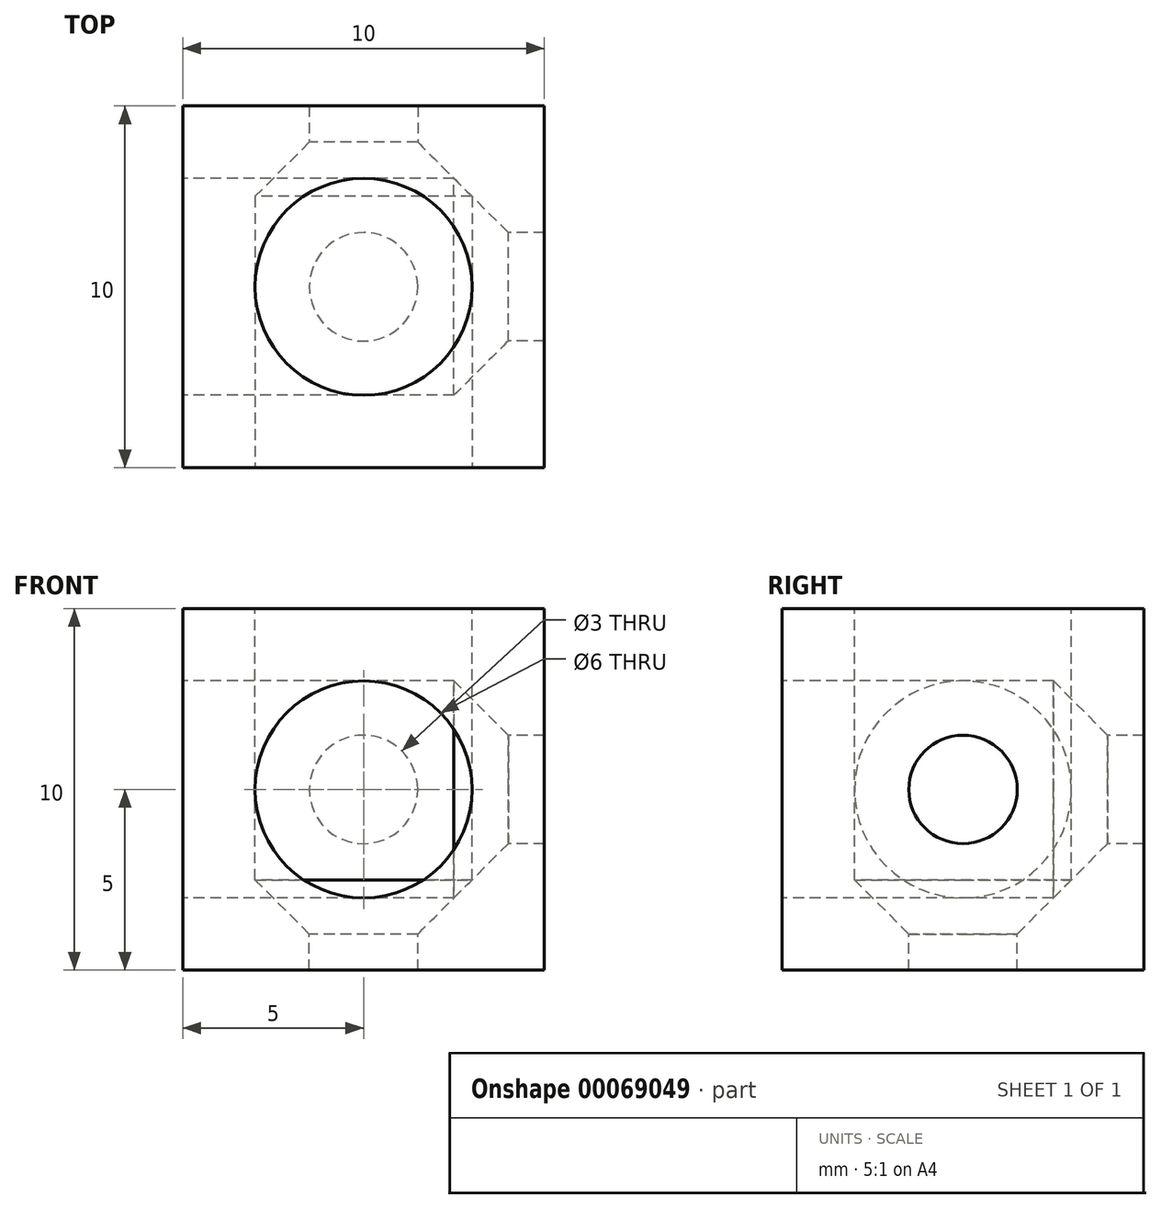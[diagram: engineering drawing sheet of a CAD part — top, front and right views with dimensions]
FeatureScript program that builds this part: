
annotation { "Feature Type Name" : "Feature", "Feature Type Description" : "" }
export const myFeature = defineFeature(function(context is Context, id is Id, definition is map)
    precondition{}
    {
        {
            var Q0;
            Q0=qCreatedBy(makeId("Front.planeOp"),FACE);
            var sketch = newSketch(context, id + "F0", { "sketchPlane" : qUnion([Q0])});
            skLineSegment(sketch, "E0.rect.bottom", {"start": v(5, 5) * mm, "end": v(-5, 5) * mm});
            skLineSegment(sketch, "E0.rect.top", {"start": v(5, -5) * mm, "end": v(-5, -5) * mm});
            skLineSegment(sketch, "E0.rect.left", {"start": v(5, 5) * mm, "end": v(5, -5) * mm});
            skLineSegment(sketch, "E0.rect.right", {"start": v(-5, 5) * mm, "end": v(-5, -5) * mm});
            skPoint(sketch, "E0.rect.middle", {"position": v(0, 0) * mm});
            skSolve(sketch);
        }
        {
            var Q0;
            Q0=makeQuery(id+"F0.imprint","IMPRINT",FACE,{"disambiguationData":[TD([[makeQuery(id+"F0.imprint","IMPRINT",EDGE,{"derivedFrom":sQuery(id+"F0.wireOp",EDGE,"E0.rect.bottom")}),1.0]])]});
            extrude(context, id + "F1", {"entities" : qUnion([Q0]), "endBound" : BoundingType.SYMMETRIC, "depth" : 10 * mm});
        }
        {
            var Q0;
            Q0=qCreatedBy(makeId("Front.planeOp"),FACE);
            var sketch = newSketch(context, id + "F2", { "sketchPlane" : qUnion([Q0])});
            skLineSegment(sketch, "E1", {"start": v(0, 5) * mm, "end": v(0, -5) * mm});
            skLineSegment(sketch, "E2", {"start": v(0, -5) * mm, "end": v(1.5, -5) * mm});
            skLineSegment(sketch, "E3", {"start": v(1.5, -5) * mm, "end": v(1.5, -4) * mm});
            skLineSegment(sketch, "E4", {"start": v(1.5, -4) * mm, "end": v(3, -2.5) * mm});
            skLineSegment(sketch, "E5", {"start": v(3, -2.5) * mm, "end": v(3, 5) * mm});
            skLineSegment(sketch, "E6", {"start": v(3, 5) * mm, "end": v(0, 5) * mm});
            skLineSegment(sketch, "E7", {"start": v(0, 0) * mm, "end": v(8.33, 0) * mm, "construction": true});
            skSolve(sketch);
        }
        {
            var Q0;
            Q0=makeQuery(id+"F2.imprint","IMPRINT",FACE,{"disambiguationData":[TD([[makeQuery(id+"F2.imprint","IMPRINT",EDGE,{"derivedFrom":sQuery(id+"F2.wireOp",EDGE,"E1")}),1.0]])]});
            var Q1;
            Q1=sQuery(id+"F2.wireOp",EDGE,"E1");
            revolve(context, id + "F3", {"entities" : qUnion([Q0]), "axis" : qUnion([Q1]), "revolveType" : RevolveType.FULL});
        }
        {
            var Q0;
            Q0=makeQuery(id+"F3.opRevolve","SWEPT_BODY",BODY,{"disambiguationData":[OSD([sQuery(id+"F2.wireOp",EDGE,"E1"),sQuery(id+"F2.wireOp",EDGE,"E2"),sQuery(id+"F2.wireOp",EDGE,"E3"),sQuery(id+"F2.wireOp",EDGE,"E4"),sQuery(id+"F2.wireOp",EDGE,"E5"),sQuery(id+"F2.wireOp",EDGE,"E6")])]});
            var Q1;
            Q1=sQuery(id+"F2.wireOp",EDGE,"E7");
            transform(context, id + "F4", {"entities" : qUnion([Q0]), "transformType" : TransformType.ROTATION, "transformAxis" : qUnion([Q1]), "angle" : 90 * degree, "makeCopy" : true});
        }
        {
            var Q0;
            Q0=makeQuery(id+"F4.opPattern","COPY",BODY,{"derivedFrom":makeQuery(id+"F3.opRevolve","SWEPT_BODY",BODY,{"disambiguationData":[OSD([sQuery(id+"F2.wireOp",EDGE,"E1"),sQuery(id+"F2.wireOp",EDGE,"E2"),sQuery(id+"F2.wireOp",EDGE,"E3"),sQuery(id+"F2.wireOp",EDGE,"E4"),sQuery(id+"F2.wireOp",EDGE,"E5"),sQuery(id+"F2.wireOp",EDGE,"E6")])]}),"instanceName":"1"});
            var Q1;
            Q1=sQuery(id+"F2.wireOp",EDGE,"E1");
            transform(context, id + "F5", {"entities" : qUnion([Q0]), "transformType" : TransformType.ROTATION, "transformAxis" : qUnion([Q1]), "angle" : 90 * degree, "makeCopy" : true});
        }
        {
            var Q0;
            Q0=makeQuery(id+"F4.opPattern","COPY",BODY,{"derivedFrom":makeQuery(id+"F3.opRevolve","SWEPT_BODY",BODY,{"disambiguationData":[OSD([sQuery(id+"F2.wireOp",EDGE,"E1"),sQuery(id+"F2.wireOp",EDGE,"E2"),sQuery(id+"F2.wireOp",EDGE,"E3"),sQuery(id+"F2.wireOp",EDGE,"E4"),sQuery(id+"F2.wireOp",EDGE,"E5"),sQuery(id+"F2.wireOp",EDGE,"E6")])]}),"instanceName":"1"});
            var Q1;
            Q1=makeQuery(id+"F1.opExtrude","SWEPT_BODY",BODY,{"disambiguationData":[OSD([sQuery(id+"F0.wireOp",EDGE,"E0.rect.bottom"),sQuery(id+"F0.wireOp",EDGE,"E0.rect.top"),sQuery(id+"F0.wireOp",EDGE,"E0.rect.left"),sQuery(id+"F0.wireOp",EDGE,"E0.rect.right")])]});
            booleanBodies(context, id + "F6", {"operationType" : BooleanOperationType.SUBTRACTION, "tools" : qUnion([Q0]), "targets" : qUnion([Q1])});
        }
    });
